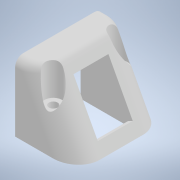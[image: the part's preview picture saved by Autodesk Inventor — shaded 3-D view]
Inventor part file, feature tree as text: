
AUTODESK INVENTOR PART (.ipt)
format: ipt  version: 2021 (Build 250183000, 183)  size: 202,752 bytes
history: native  units: mm
features: extrude x5, sketch x4, fillet x2, projected_geometry x1
ambient origin geometry x8: Origin, YZ Plane, XZ Plane, XY Plane, X Axis, Y Axis, Z Axis, Center Point
bodies: Solid1 (feature_tree)
feature tree (12):
  extrude  "Extrusion1"  Depth=20.591395mm
  extrude  "Extrusion2"  Depth=32.0mm TaperAngle=0.0deg
  sketch  "Sketch3"  dims[d7=16.0mm d8=0.0mm d9=3.0mm]
  fillet  "Fillet1"  Radius=2.0mm
  fillet  "Fillet2"  Radius=2.0mm
  extrude  "Extrusion3"  Depth=3.0mm
  sketch  "Sketch4"  dims[d10=8.0mm d11=12.8mm d12=19.0mm d13=0.0mm d14=0.0mm d15=12.0mm d16=12.0mm d17=10.0mm d18=3.2mm d19=6.5mm d20=0.0mm d21=0.0mm d22=12.0mm d23=0.0mm]
  extrude  "Extrusion4"  Depth=10.0mm
  extrude  "Extrusion5"  Depth=10.0mm
  sketch  "Sketch1"  dims[d0=22.895mm d1=20.591395mm]
  sketch  "Sketch2"  dims[d2=25.0mm d3=32.0mm d4=0.0mm d5=2.0mm d6=2.0mm]
  projected_geometry  "Projected Loop1"
